# Revit family: Detector de Fumaça SDO ILUMAC
name_source: partatom
category: Dispositivos de alarme de incêndio
units: mm (PartAtom-declared; Revit-internal decimal feet)

## family parameters
Com base no plano de trabalho = Não
Compartilhado = Não
Corte com vazios quando carregada = Não
Cota do conector redondo = Utilizar diâmetro
Manter orientação da anotação = Não
Número OmniClass = 23.75.00.00
Ponto de cálculo do ambiente = Não
Sempre na vertical = Sim
Tipo de parte = Normal
Título OmniClass = Climate Control (HVAC)

## types (10) — shared parameters
Altura máxima de instalação = 8m*
Dimensões (AxLxP) = 98mm de diâmetro e 45mm de profund. (com a base)
Fabricante = ILUMAC
Fixação = Base de sobrepor c/ terminais p/ conexão dos cabos
Grau de proteção = IP20 (uso interno)
Normas técnicas aplicáveis = NBR 17240 | ISO 7240-7
Nível de reposta = 0,08 à 0,15 dB/m
Sensibilidade = 4,0 à 4,3% / ft
Temperatura de operação = -5ºC a +57ºC
Tempo de inicialização = 15 segundos
Tempo de resposta = 03 segundos
Tensão nominal = 24VCC
Tipo de detecção = Fumaça – por câmara óptica IRED
Área de cobertura = 81m2
zero-valued in all types: Elevação padrão

## per-type parameters (varying)
| type | Consumo | Código do produto | Descrição | Endereços programáveis | Endereços utilizados | Material da caixa | Níveis de acionamento | PLASTICO ABS | Peso | Protocolo de comunicação A | Tensão de operação | Umidade relativa |
| SDO-C BRANCO | 90uA em supervisão
30mA em alarme | 0010017 | Detector de Fumaça Convencional SDO-C branco |  |  | Plástico ABS branco |  | ABS BRANCO | 130g |  | 20 a 28VCC | (0 a 95% (sem condensação) |
| SDO-C PRETO | 90uA em supervisão
30mA em alarme | 0010020 | Detector de Fumaça Convencional SDO-C preto |  |  | Plástico ABS preto |  | PLÁSTICO PRETO | 130g |  | 20 a 28VCC | (0 a 95% (sem condensação) |
| SDO-E BRANCO | 400uA em supervisão
1,3mA em alarme | 0020029 | Detector de Fumaça Endereçável SDO-E branco | 001 a 500 | 1 endereço | Plástico ABS branco |  | ABS BRANCO | 150g | ALF-500 (proprietário) | 22 a 28VCC | a 0 a 95% (sem condensação) |
| SDO-E PRETO | 400uA em supervisão
1,3mA em alarme | 0020028 | Detector de Fumaça Endereçável SDO-E preto | 001 a 500 | 1 endereço | Plástico ABS preto |  | PLÁSTICO PRETO | 150g | ALF-500 (proprietário) | 22 a 28VCC | a 0 a 95% (sem condensação) |
| SDO-D BRANCO | 900uA em supervisão
1,8mA em alarme | 0040021 | Detector de Fumaça Óptico Endereçável Sirius SDO-D branco | 001 a 125 (por laço) | 1 endereço | Plástico ABS branco |  | ABS BRANCO | 150g | ALF-1000-2 (proprietário) | 20 a 30VCC | a 0 a 95% (sem condensação) |
| SDO-A BRANCO | 900uA em supervisão
1,8mA em alarme | 0040050 | Detector de Fumaça Óptico Analógico Sirius SDO-A branco | 001 a 125 (por laço) | 1 endereço | Plástico ABS branco | Ajustados individualmente na central em até 3 níveis
de sensibilidade: Baixa / Média (Padrão) / Alta | ABS BRANCO | 150g | ALF-1000-2 | 20 a 30VCC | a 0 a 95% (sem condensação) |
| SDO-A PRETO | 900uA em supervisão
1,8mA em alarme | 0040050 | Detector de Fumaça Óptico Analógico Sirius SDO-A preto | 001 a 125 (por laço) | 1 endereço | Plástico ABS preto | Ajustados individualmente na central em até 3 níveis
de sensibilidade: Baixa / Média (Padrão) / Alta | PLÁSTICO PRETO | 150g | ALF-1000-2 | 20 a 30VCC | a 0 a 95% (sem condensação) |
| SDO-D PRETO | 900uA em supervisão
1,8mA em alarme | 0040021 | Detector de Fumaça Óptico Endereçável Sirius SDO-D preto | 001 a 125 (por laço) | 1 endereço | Plástico ABS preto |  | PLÁSTICO PRETO | 150g | ALF-1000-2 (proprietário) | 20 a 30VCC | a 0 a 95% (sem condensação) |
| SDO-G BRANCO | 850uA em supervisão
1,9mA em alarme | 007045 | Detector de Fumaça Óptico Endereçável Cygnus SDO-G branco | 001 a 125 (por laço) | 1 endereço | Plástico ABS branco |  | ABS BRANCO | 150g | CYGNUS (proprietário) | 20 a 30VCC | 0 a 95% (sem condensação) |
| SDO-G PRETO | 850uA em supervisão
1,9mA em alarme | 007046 | Detector de Fumaça Óptico Endereçável Cygnus SDO-G preto | 001 a 125 (por laço) | 1 endereço | Plástico ABS preto |  | ABS BRANCO | 150g | CYGNUS (proprietário) | 20 a 30VCC | 0 a 95% (sem condensação) |

note: column(s) folded — value = type name in every type: Modelo
